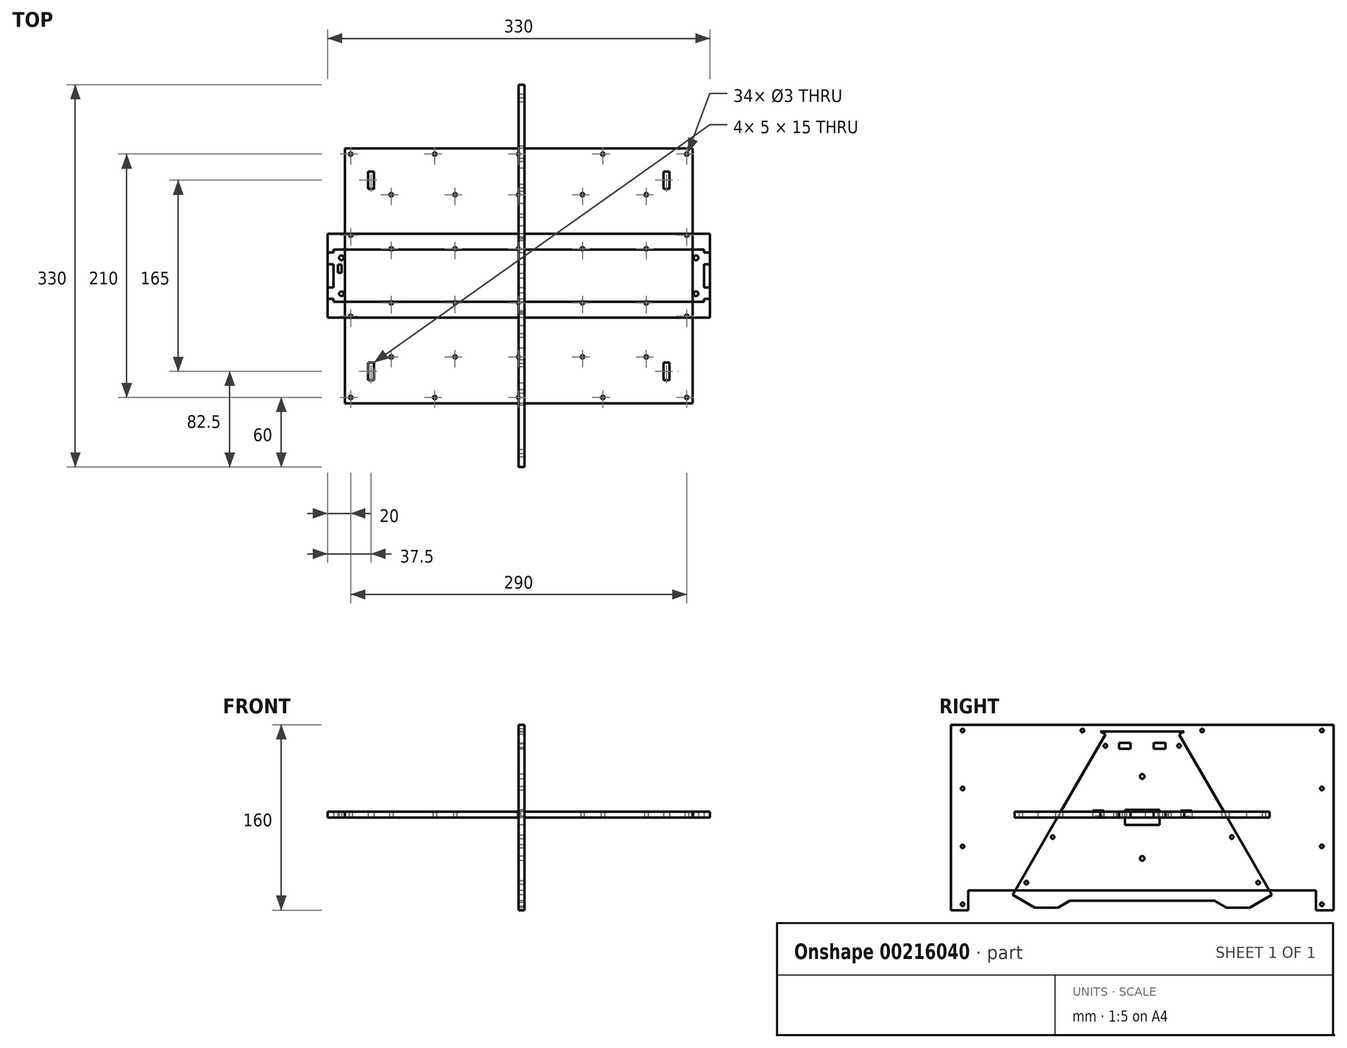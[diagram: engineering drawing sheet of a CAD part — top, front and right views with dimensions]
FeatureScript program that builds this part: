
annotation { "Feature Type Name" : "Feature", "Feature Type Description" : "" }
export const myFeature = defineFeature(function(context is Context, id is Id, definition is map)
    precondition{}
    {
        {
            var Q0;
            Q0=qCreatedBy(makeId("Top.planeOp"),FACE);
            var sketch = newSketch(context, id + "F0", { "sketchPlane" : qUnion([Q0])});
            skLineSegment(sketch, "E0.bottom", {"start": v(150, -110) * mm, "end": v(-150, -110) * mm});
            skLineSegment(sketch, "E0.top", {"start": v(150, 110) * mm, "end": v(-150, 110) * mm});
            skLineSegment(sketch, "E0.left", {"start": v(150, -110) * mm, "end": v(150, 110) * mm});
            skLineSegment(sketch, "E0.right", {"start": v(-150, -110) * mm, "end": v(-150, 110) * mm});
            skPoint(sketch, "E0.middle", {"position": v(0, 0) * mm});
            skCircle(sketch, "E1", {"center": v(-145, 105) * mm, "radius": 1.5 * mm});
            skCircle(sketch, "E2.0.1.0", {"center": v(-145, -105) * mm, "radius": 1.5 * mm});
            skCircle(sketch, "E2.1.0.0", {"center": v(-72.5, 105) * mm, "radius": 1.5 * mm});
            skCircle(sketch, "E2.1.1.0", {"center": v(-72.5, -105) * mm, "radius": 1.5 * mm});
            skCircle(sketch, "E2.2.0.0", {"center": v(0, 105) * mm, "radius": 1.5 * mm});
            skCircle(sketch, "E2.2.1.0", {"center": v(0, -105) * mm, "radius": 1.5 * mm});
            skCircle(sketch, "E2.3.0.0", {"center": v(72.5, 105) * mm, "radius": 1.5 * mm});
            skCircle(sketch, "E2.3.1.0", {"center": v(72.5, -105) * mm, "radius": 1.5 * mm});
            skCircle(sketch, "E2.4.0.0", {"center": v(145, 105) * mm, "radius": 1.5 * mm});
            skCircle(sketch, "E2.4.1.0", {"center": v(145, -105) * mm, "radius": 1.5 * mm});
            skLineSegment(sketch, "E2.direction1", {"start": v(-145, 105) * mm, "end": v(-72.5, 105) * mm, "construction": true});
            skLineSegment(sketch, "E2.direction2", {"start": v(-145, 105) * mm, "end": v(-145, -105) * mm, "construction": true});
            skCircle(sketch, "E3", {"center": v(-145, -35) * mm, "radius": 1.5 * mm});
            skCircle(sketch, "E4.0.1.0", {"center": v(-145, 35) * mm, "radius": 1.5 * mm});
            skCircle(sketch, "E4.1.0.0", {"center": v(145, -35) * mm, "radius": 1.5 * mm});
            skCircle(sketch, "E4.1.1.0", {"center": v(145, 35) * mm, "radius": 1.5 * mm});
            skLineSegment(sketch, "E4.direction1", {"start": v(-145, -35) * mm, "end": v(145, -35) * mm, "construction": true});
            skLineSegment(sketch, "E4.direction2", {"start": v(-145, -35) * mm, "end": v(-145, 35) * mm, "construction": true});
            skLineSegment(sketch, "E5", {"start": v(-87.87, 0) * mm, "end": v(86.7, 0) * mm, "construction": true});
            skLineSegment(sketch, "E6", {"start": v(0, -57.45) * mm, "end": v(0, 56.94) * mm, "construction": true});
            skLineSegment(sketch, "E7", {"start": v(145, 35) * mm, "end": v(145, 105) * mm, "construction": true});
            skLineSegment(sketch, "E8.bottom", {"start": v(-130, -75) * mm, "end": v(-125, -75) * mm});
            skLineSegment(sketch, "E8.top", {"start": v(-130, -90) * mm, "end": v(-125, -90) * mm});
            skLineSegment(sketch, "E8.left", {"start": v(-130, -75) * mm, "end": v(-130, -90) * mm});
            skLineSegment(sketch, "E8.right", {"start": v(-125, -75) * mm, "end": v(-125, -90) * mm});
            skLineSegment(sketch, "E9.0.1.0", {"start": v(-130, 90) * mm, "end": v(-130, 75) * mm});
            skLineSegment(sketch, "E9.0.1.1", {"start": v(-130, 75) * mm, "end": v(-125, 75) * mm});
            skLineSegment(sketch, "E9.0.1.2", {"start": v(-125, 90) * mm, "end": v(-125, 75) * mm});
            skLineSegment(sketch, "E9.0.1.3", {"start": v(-130, 90) * mm, "end": v(-125, 90) * mm});
            skLineSegment(sketch, "E9.1.0.0", {"start": v(125, -75) * mm, "end": v(125, -90) * mm});
            skLineSegment(sketch, "E9.1.0.1", {"start": v(125, -90) * mm, "end": v(130, -90) * mm});
            skLineSegment(sketch, "E9.1.0.2", {"start": v(130, -75) * mm, "end": v(130, -90) * mm});
            skLineSegment(sketch, "E9.1.0.3", {"start": v(125, -75) * mm, "end": v(130, -75) * mm});
            skLineSegment(sketch, "E9.1.1.0", {"start": v(125, 90) * mm, "end": v(125, 75) * mm});
            skLineSegment(sketch, "E9.1.1.1", {"start": v(125, 75) * mm, "end": v(130, 75) * mm});
            skLineSegment(sketch, "E9.1.1.2", {"start": v(130, 90) * mm, "end": v(130, 75) * mm});
            skLineSegment(sketch, "E9.1.1.3", {"start": v(125, 90) * mm, "end": v(130, 90) * mm});
            skLineSegment(sketch, "E9.direction1", {"start": v(-130, -90) * mm, "end": v(125, -90) * mm, "construction": true});
            skLineSegment(sketch, "E9.direction2", {"start": v(-130, -90) * mm, "end": v(-130, 75) * mm, "construction": true});
            skCircle(sketch, "E10", {"center": v(-110, 70) * mm, "radius": 1.5 * mm});
            skCircle(sketch, "E11.0.1.0", {"center": v(-110, 23.33) * mm, "radius": 1.5 * mm});
            skCircle(sketch, "E11.0.2.0", {"center": v(-110, -23.33) * mm, "radius": 1.5 * mm});
            skCircle(sketch, "E11.0.3.0", {"center": v(-110, -70) * mm, "radius": 1.5 * mm});
            skCircle(sketch, "E11.1.0.0", {"center": v(-55, 70) * mm, "radius": 1.5 * mm});
            skCircle(sketch, "E11.1.1.0", {"center": v(-55, 23.33) * mm, "radius": 1.5 * mm});
            skCircle(sketch, "E11.1.2.0", {"center": v(-55, -23.33) * mm, "radius": 1.5 * mm});
            skCircle(sketch, "E11.1.3.0", {"center": v(-55, -70) * mm, "radius": 1.5 * mm});
            skCircle(sketch, "E11.2.0.0", {"center": v(0, 70) * mm, "radius": 1.5 * mm});
            skCircle(sketch, "E11.2.1.0", {"center": v(0, 23.33) * mm, "radius": 1.5 * mm});
            skCircle(sketch, "E11.2.2.0", {"center": v(0, -23.33) * mm, "radius": 1.5 * mm});
            skCircle(sketch, "E11.2.3.0", {"center": v(0, -70) * mm, "radius": 1.5 * mm});
            skCircle(sketch, "E11.3.0.0", {"center": v(55, 70) * mm, "radius": 1.5 * mm});
            skCircle(sketch, "E11.3.1.0", {"center": v(55, 23.33) * mm, "radius": 1.5 * mm});
            skCircle(sketch, "E11.3.2.0", {"center": v(55, -23.33) * mm, "radius": 1.5 * mm});
            skCircle(sketch, "E11.3.3.0", {"center": v(55, -70) * mm, "radius": 1.5 * mm});
            skCircle(sketch, "E11.4.0.0", {"center": v(110, 70) * mm, "radius": 1.5 * mm});
            skCircle(sketch, "E11.4.1.0", {"center": v(110, 23.33) * mm, "radius": 1.5 * mm});
            skCircle(sketch, "E11.4.2.0", {"center": v(110, -23.33) * mm, "radius": 1.5 * mm});
            skCircle(sketch, "E11.4.3.0", {"center": v(110, -70) * mm, "radius": 1.5 * mm});
            skLineSegment(sketch, "E11.direction1", {"start": v(-110, 70) * mm, "end": v(-55, 70) * mm, "construction": true});
            skLineSegment(sketch, "E11.direction2", {"start": v(-110, 70) * mm, "end": v(-110, 23.33) * mm, "construction": true});
            skSolve(sketch);
        }
        {
            var Q0;
            Q0=makeQuery(id+"F0.imprint","IMPRINT",FACE,{"disambiguationData":[TD([[makeQuery(id+"F0.imprint","IMPRINT",EDGE,{"derivedFrom":sQuery(id+"F0.wireOp",EDGE,"E0.bottom")}),-1.0]])]});
            extrude(context, id + "F1", {"entities" : qUnion([Q0]), "depth" : 5 * mm});
        }
        {
            var Q0;
            Q0=qCreatedBy(makeId("Right.planeOp"),FACE);
            var sketch = newSketch(context, id + "F2", { "sketchPlane" : qUnion([Q0])});
            skLineSegment(sketch, "E12", {"start": v(-31.8, 71.78) * mm, "end": v(31.8, 71.78) * mm});
            skLineSegment(sketch, "E13", {"start": v(31.8, 71.78) * mm, "end": v(111.83, -66.78) * mm});
            skLineSegment(sketch, "E14", {"start": v(111.83, -66.78) * mm, "end": v(103.17, -71.78) * mm});
            skLineSegment(sketch, "E15", {"start": v(103.17, -71.78) * mm, "end": v(-103.17, -71.78) * mm});
            skLineSegment(sketch, "E16", {"start": v(-103.17, -71.78) * mm, "end": v(-111.83, -66.78) * mm});
            skLineSegment(sketch, "E17", {"start": v(-111.83, -66.78) * mm, "end": v(-31.8, 71.78) * mm});
            skLineSegment(sketch, "E18", {"start": v(0, -71.78) * mm, "end": v(0, 71.78) * mm, "construction": true});
            skCircle(sketch, "E19", {"center": v(31.8, 61.78) * mm, "radius": 1.5 * mm});
            skLineSegment(sketch, "E20", {"start": v(31.8, 61.78) * mm, "end": v(36.13, 64.28) * mm, "construction": true});
            skCircle(sketch, "E21.1.0.0", {"center": v(54.54, 22.43) * mm, "radius": 1.5 * mm, "construction": true});
            skCircle(sketch, "E21.2.0.0", {"center": v(77.27, -16.93) * mm, "radius": 1.5 * mm});
            skCircle(sketch, "E21.3.0.0", {"center": v(100, -56.3) * mm, "radius": 1.5 * mm});
            skLineSegment(sketch, "E21.direction1", {"start": v(31.8, 61.78) * mm, "end": v(54.54, 22.43) * mm, "construction": true});
            skLineSegment(sketch, "E22", {"start": v(100, -56.3) * mm, "end": v(107.5, -69.28) * mm, "construction": true});
            skCircle(sketch, "E23", {"center": v(-31.8, 61.78) * mm, "radius": 1.5 * mm});
            skCircle(sketch, "E24.1.0.0", {"center": v(-54.54, 22.43) * mm, "radius": 1.5 * mm, "construction": true});
            skCircle(sketch, "E24.2.0.0", {"center": v(-77.27, -16.93) * mm, "radius": 1.5 * mm});
            skCircle(sketch, "E24.3.0.0", {"center": v(-100, -56.3) * mm, "radius": 1.5 * mm});
            skLineSegment(sketch, "E24.direction1", {"start": v(-31.8, 61.78) * mm, "end": v(-54.54, 22.43) * mm, "construction": true});
            skLineSegment(sketch, "E25", {"start": v(-100, -56.3) * mm, "end": v(-107.5, -69.28) * mm, "construction": true});
            skCircle(sketch, "E26", {"center": v(0, 0) * mm, "radius": 35.35 * mm, "construction": true});
            skCircle(sketch, "E27", {"center": v(0, 35.35) * mm, "radius": 2 * mm});
            skCircle(sketch, "E28", {"center": v(0, -35.35) * mm, "radius": 2 * mm});
            skLineSegment(sketch, "E29", {"start": v(-103.17, -71.78) * mm, "end": v(-92.78, -77.78) * mm});
            skLineSegment(sketch, "E30", {"start": v(-92.78, -77.78) * mm, "end": v(-72.78, -77.78) * mm});
            skLineSegment(sketch, "E31", {"start": v(-72.78, -77.78) * mm, "end": v(-62.4, -71.78) * mm});
            skLineSegment(sketch, "E32", {"start": v(103.17, -71.78) * mm, "end": v(92.78, -77.78) * mm});
            skLineSegment(sketch, "E33", {"start": v(92.78, -77.78) * mm, "end": v(72.78, -77.78) * mm});
            skLineSegment(sketch, "E34", {"start": v(72.78, -77.78) * mm, "end": v(62.4, -71.78) * mm});
            skLineSegment(sketch, "E35", {"start": v(-31.8, 71.78) * mm, "end": v(-36.13, 74.28) * mm});
            skLineSegment(sketch, "E36", {"start": v(31.8, 71.78) * mm, "end": v(36.13, 74.28) * mm});
            skLineSegment(sketch, "E37", {"start": v(-36.13, 74.28) * mm, "end": v(36.13, 74.28) * mm});
            skLineSegment(sketch, "E38.bottom", {"start": v(33, 6) * mm, "end": v(43, 6) * mm});
            skLineSegment(sketch, "E38.top", {"start": v(33, 1) * mm, "end": v(43, 1) * mm});
            skLineSegment(sketch, "E38.left", {"start": v(33, 6) * mm, "end": v(33, 1) * mm});
            skLineSegment(sketch, "E38.right", {"start": v(43, 6) * mm, "end": v(43, 1) * mm});
            skLineSegment(sketch, "E39.bottom", {"start": v(-33, 6) * mm, "end": v(-43, 6) * mm});
            skLineSegment(sketch, "E39.top", {"start": v(-33, 1) * mm, "end": v(-43, 1) * mm});
            skLineSegment(sketch, "E39.left", {"start": v(-33, 6) * mm, "end": v(-33, 1) * mm});
            skLineSegment(sketch, "E39.right", {"start": v(-43, 6) * mm, "end": v(-43, 1) * mm});
            skLineSegment(sketch, "E40", {"start": v(-23.31, 0) * mm, "end": v(25.56, 0) * mm, "construction": true});
            skLineSegment(sketch, "E41.bottom", {"start": v(15, -6.5) * mm, "end": v(-15, -6.5) * mm});
            skLineSegment(sketch, "E41.top", {"start": v(15, 6.5) * mm, "end": v(-15, 6.5) * mm});
            skLineSegment(sketch, "E41.left", {"start": v(15, -6.5) * mm, "end": v(15, 6.5) * mm});
            skLineSegment(sketch, "E41.right", {"start": v(-15, -6.5) * mm, "end": v(-15, 6.5) * mm});
            skLineSegment(sketch, "E42.bottom", {"start": v(-15, -6.5) * mm, "end": v(-4, -6.5) * mm});
            skLineSegment(sketch, "E42.top", {"start": v(-15, 0) * mm, "end": v(-4, 0) * mm});
            skLineSegment(sketch, "E42.left", {"start": v(-15, -6.5) * mm, "end": v(-15, 0) * mm});
            skLineSegment(sketch, "E42.right", {"start": v(-4, -6.5) * mm, "end": v(-4, 0) * mm});
            skSolve(sketch);
        }
        {
            var Q0;
            Q0=makeQuery(id+"F2.imprint","IMPRINT",FACE,{"disambiguationData":[TD([[makeQuery(id+"F2.imprint","IMPRINT",EDGE,{"derivedFrom":sQuery(id+"F2.wireOp",EDGE,"E12")}),-1.0]])]});
            var Q1;
            {var subQ0=sQuery(id+"F2.wireOp",EDGE,"E29");Q1=makeQuery(id+"F2.imprint","IMPRINT",FACE,{"disambiguationData":[TD([[makeQuery(id+"F2.imprint","IMPRINT",EDGE,{"derivedFrom":subQ0}),1.0]])]});}
            var Q2;
            {var subQ0=sQuery(id+"F2.wireOp",EDGE,"E32");Q2=makeQuery(id+"F2.imprint","IMPRINT",FACE,{"disambiguationData":[TD([[makeQuery(id+"F2.imprint","IMPRINT",EDGE,{"derivedFrom":subQ0}),-1.0]])]});}
            var Q3;
            Q3=makeQuery(id+"F2.imprint","IMPRINT",FACE,{"disambiguationData":[TD([[makeQuery(id+"F2.imprint","IMPRINT",EDGE,{"derivedFrom":sQuery(id+"F2.wireOp",EDGE,"E12")}),1.0]])]});
            var Q4;
            Q4=makeQuery(id+"F2.imprint","IMPRINT",FACE,{"disambiguationData":[TD([[makeQuery(id+"F2.imprint","IMPRINT",EDGE,{"derivedFrom":sQuery(id+"F2.wireOp",EDGE,"1zBQG6Iy-hJ6P-1aGQ-Iii5-wYXhp56Ifulz.bottom")}),-1.0]])]});
            var Q5;
            Q5=makeQuery(id+"F2.imprint","IMPRINT",FACE,{"disambiguationData":[TD([[makeQuery(id+"F2.imprint","IMPRINT",EDGE,{"derivedFrom":sQuery(id+"F2.wireOp",EDGE,"E42.bottom")}),1.0]])]});
            extrude(context, id + "F3", {"entities" : qUnion([Q0, Q1, Q2, Q3, Q4, Q5]), "depth" : 5 * mm});
        }
        {
            var Q0;
            Q0=qCreatedBy(makeId("Right.planeOp"),FACE);
            var sketch = newSketch(context, id + "F4", { "sketchPlane" : qUnion([Q0])});
            skLineSegment(sketch, "E43", {"start": v(-165, 80) * mm, "end": v(165, 80) * mm});
            skLineSegment(sketch, "E44", {"start": v(165, 80) * mm, "end": v(165, -80) * mm});
            skLineSegment(sketch, "E45", {"start": v(165, -80) * mm, "end": v(150, -80) * mm});
            skLineSegment(sketch, "E46", {"start": v(150, -80) * mm, "end": v(150, -63) * mm});
            skLineSegment(sketch, "E47", {"start": v(150, -63) * mm, "end": v(-150, -63) * mm});
            skLineSegment(sketch, "E48", {"start": v(-150, -63) * mm, "end": v(-150, -80) * mm});
            skLineSegment(sketch, "E49", {"start": v(-150, -80) * mm, "end": v(-165, -80) * mm});
            skLineSegment(sketch, "E50", {"start": v(-165, -80) * mm, "end": v(-165, 80) * mm});
            skLineSegment(sketch, "E51", {"start": v(0, 153.24) * mm, "end": v(0, -118.2) * mm, "construction": true});
            skLineSegment(sketch, "E52", {"start": v(-243.49, 0) * mm, "end": v(242.88, 0) * mm, "construction": true});
            skCircle(sketch, "E53", {"center": v(155, -75) * mm, "radius": 1.5 * mm});
            skCircle(sketch, "E54", {"center": v(-155, -75) * mm, "radius": 1.5 * mm});
            skCircle(sketch, "E55.1.0.0", {"center": v(155, -25) * mm, "radius": 1.5 * mm});
            skCircle(sketch, "E55.2.0.0", {"center": v(155, 25) * mm, "radius": 1.5 * mm});
            skCircle(sketch, "E55.3.0.0", {"center": v(155, 75) * mm, "radius": 1.5 * mm});
            skLineSegment(sketch, "E55.direction1", {"start": v(155, -75) * mm, "end": v(155, -25) * mm, "construction": true});
            skCircle(sketch, "E56.1.0.0", {"center": v(-155, -25) * mm, "radius": 1.5 * mm});
            skCircle(sketch, "E56.2.0.0", {"center": v(-155, 25) * mm, "radius": 1.5 * mm});
            skCircle(sketch, "E56.3.0.0", {"center": v(-155, 75) * mm, "radius": 1.5 * mm});
            skLineSegment(sketch, "E56.direction1", {"start": v(-155, -75) * mm, "end": v(-155, -25) * mm, "construction": true});
            skCircle(sketch, "E57.1.0.0", {"center": v(-51.67, 75) * mm, "radius": 1.5 * mm});
            skCircle(sketch, "E57.2.0.0", {"center": v(51.67, 75) * mm, "radius": 1.5 * mm});
            skLineSegment(sketch, "E57.direction1", {"start": v(-155, 75) * mm, "end": v(-51.67, 75) * mm, "construction": true});
            skLineSegment(sketch, "E58", {"start": v(51.67, 75) * mm, "end": v(155, 75) * mm, "construction": true});
            skSolve(sketch);
        }
        {
            var Q0;
            Q0=makeQuery(id+"F4.imprint","IMPRINT",FACE,{"disambiguationData":[TD([[makeQuery(id+"F4.imprint","IMPRINT",EDGE,{"derivedFrom":sQuery(id+"F4.wireOp",EDGE,"E43")}),-1.0]])]});
            extrude(context, id + "F5", {"entities" : qUnion([Q0]), "depth" : 5 * mm});
        }
        {
            var Q0;
            Q0=makeQuery(id+"F3.opExtrude","CAP_FACE",FACE,{"disambiguationData":[OSD([sQuery(id+"F2.wireOp",EDGE,"E13"),sQuery(id+"F2.wireOp",EDGE,"E14"),sQuery(id+"F2.wireOp",EDGE,"E15"),sQuery(id+"F2.wireOp",EDGE,"E16"),sQuery(id+"F2.wireOp",EDGE,"E17"),sQuery(id+"F2.wireOp",EDGE,"E19"),sQuery(id+"F2.wireOp",EDGE,"E21.2.0.0"),sQuery(id+"F2.wireOp",EDGE,"E21.3.0.0"),sQuery(id+"F2.wireOp",EDGE,"E23"),sQuery(id+"F2.wireOp",EDGE,"E24.2.0.0"),sQuery(id+"F2.wireOp",EDGE,"E24.3.0.0"),sQuery(id+"F2.wireOp",EDGE,"O3QZEwBj-KtqO-yXGe-cdQq-akg9gxT5v1oA"),sQuery(id+"F2.wireOp",EDGE,"E27"),sQuery(id+"F2.wireOp",EDGE,"E28"),sQuery(id+"F2.wireOp",EDGE,"E29"),sQuery(id+"F2.wireOp",EDGE,"E30"),sQuery(id+"F2.wireOp",EDGE,"E31"),sQuery(id+"F2.wireOp",EDGE,"E32"),sQuery(id+"F2.wireOp",EDGE,"E33"),sQuery(id+"F2.wireOp",EDGE,"E34"),sQuery(id+"F2.wireOp",EDGE,"E35"),sQuery(id+"F2.wireOp",EDGE,"E36"),sQuery(id+"F2.wireOp",EDGE,"E37")])],"isStart":false});
            var sketch = newSketch(context, id + "F6", { "sketchPlane" : qUnion([Q0])});
            skLineSegment(sketch, "E59.bottom", {"start": v(10, 64.28) * mm, "end": v(20, 64.28) * mm});
            skLineSegment(sketch, "E59.top", {"start": v(10, 59.28) * mm, "end": v(20, 59.28) * mm});
            skLineSegment(sketch, "E59.left", {"start": v(10, 64.28) * mm, "end": v(10, 59.28) * mm});
            skLineSegment(sketch, "E59.right", {"start": v(20, 64.28) * mm, "end": v(20, 59.28) * mm});
            skLineSegment(sketch, "E60.bottom", {"start": v(-20, 64.28) * mm, "end": v(-10, 64.28) * mm});
            skLineSegment(sketch, "E60.top", {"start": v(-20, 59.28) * mm, "end": v(-10, 59.28) * mm});
            skLineSegment(sketch, "E60.left", {"start": v(-20, 64.28) * mm, "end": v(-20, 59.28) * mm});
            skLineSegment(sketch, "E60.right", {"start": v(-10, 64.28) * mm, "end": v(-10, 59.28) * mm});
            skLineSegment(sketch, "E61", {"start": v(0, 106.18) * mm, "end": v(0, 6.84) * mm, "construction": true});
            skSolve(sketch);
        }
        {
            var Q0;
            Q0=makeQuery(id+"F6.imprint","IMPRINT",FACE,{"disambiguationData":[TD([[makeQuery(id+"F6.imprint","IMPRINT",EDGE,{"derivedFrom":sQuery(id+"F6.wireOp",EDGE,"E59.bottom")}),-1.0]])]});
            var Q1;
            Q1=makeQuery(id+"F6.imprint","IMPRINT",FACE,{"disambiguationData":[TD([[makeQuery(id+"F6.imprint","IMPRINT",EDGE,{"derivedFrom":sQuery(id+"F6.wireOp",EDGE,"E60.bottom")}),-1.0]])]});
            extrude(context, id + "F7", {"entities" : qUnion([Q0, Q1]), "operationType" : NewBodyOperationType.REMOVE, "endBound" : BoundingType.THROUGH_ALL, "oppositeDirection" : true, "depth" : 25 * mm});
        }
        {
            var Q0;
            Q0=qCreatedBy(makeId("Top.planeOp"),FACE);
            var sketch = newSketch(context, id + "F10", { "sketchPlane" : qUnion([Q0])});
            skLineSegment(sketch, "E62.bottom", {"start": v(160, -22.5) * mm, "end": v(-160, -22.5) * mm});
            skLineSegment(sketch, "E62.top", {"start": v(160, 22.5) * mm, "end": v(-160, 22.5) * mm});
            skLineSegment(sketch, "E62.left", {"start": v(160, -22.5) * mm, "end": v(160, 22.5) * mm});
            skLineSegment(sketch, "E62.right", {"start": v(-160, -22.5) * mm, "end": v(-160, 22.5) * mm});
            skPoint(sketch, "E62.middle", {"position": v(0, 0) * mm});
            skLineSegment(sketch, "E63", {"start": v(160, 20) * mm, "end": v(165, 20) * mm});
            skLineSegment(sketch, "E64", {"start": v(165, 20) * mm, "end": v(165, 10) * mm});
            skLineSegment(sketch, "E65", {"start": v(165, 10) * mm, "end": v(160, 10) * mm});
            skLineSegment(sketch, "E66", {"start": v(160, -10) * mm, "end": v(165, -10) * mm});
            skLineSegment(sketch, "E67", {"start": v(165, -10) * mm, "end": v(165, -20) * mm});
            skLineSegment(sketch, "E68", {"start": v(165, -20) * mm, "end": v(160, -20) * mm});
            skLineSegment(sketch, "E69", {"start": v(-160, 20) * mm, "end": v(-165, 20) * mm});
            skLineSegment(sketch, "E70", {"start": v(-165, 20) * mm, "end": v(-165, 10) * mm});
            skLineSegment(sketch, "E71", {"start": v(-165, 10) * mm, "end": v(-160, 10) * mm});
            skLineSegment(sketch, "E72", {"start": v(-160, -10) * mm, "end": v(-165, -10) * mm});
            skLineSegment(sketch, "E73", {"start": v(-165, -10) * mm, "end": v(-165, -20) * mm});
            skLineSegment(sketch, "E74", {"start": v(-165, -20) * mm, "end": v(-160, -20) * mm});
            skLineSegment(sketch, "E75", {"start": v(-87.24, 0) * mm, "end": v(82.04, 0) * mm, "construction": true});
            skCircle(sketch, "E76", {"center": v(-153, 15.5) * mm, "radius": 2 * mm});
            skCircle(sketch, "E77", {"center": v(-153, -15.5) * mm, "radius": 2 * mm});
            skCircle(sketch, "E78", {"center": v(153, 15.5) * mm, "radius": 2 * mm});
            skCircle(sketch, "E79", {"center": v(153, -15.5) * mm, "radius": 2 * mm});
            skLineSegment(sketch, "E80.bottom", {"start": v(-156, 9.5) * mm, "end": v(-153, 9.5) * mm});
            skLineSegment(sketch, "E80.top", {"start": v(-156, 2.5) * mm, "end": v(-153, 2.5) * mm});
            skLineSegment(sketch, "E80.left", {"start": v(-156, 9.5) * mm, "end": v(-156, 2.5) * mm});
            skLineSegment(sketch, "E80.right", {"start": v(-153, 9.5) * mm, "end": v(-153, 2.5) * mm});
            skSolve(sketch);
        }
        {
            var Q0;
            Q0 = qSketchRegion(id + "F10", true);
            extrude(context, id + "F8", {"entities" : qUnion([Q0]), "depth" : 5 * mm});
        }
        {
            var Q0;
            Q0=qCreatedBy(makeId("Top.planeOp"),FACE);
            var sketch = newSketch(context, id + "F11", { "sketchPlane" : qUnion([Q0])});
            skLineSegment(sketch, "E81.bottom", {"start": v(165, 36.13) * mm, "end": v(-165, 36.13) * mm});
            skLineSegment(sketch, "E81.top", {"start": v(165, -36.13) * mm, "end": v(-165, -36.13) * mm});
            skLineSegment(sketch, "E81.left", {"start": v(165, 36.13) * mm, "end": v(165, -36.13) * mm});
            skLineSegment(sketch, "E81.right", {"start": v(-165, 36.13) * mm, "end": v(-165, -36.13) * mm});
            skPoint(sketch, "E81.middle", {"position": v(0, 0) * mm});
            skCircle(sketch, "E82", {"center": v(-153, 15.5) * mm, "radius": 2 * mm});
            skCircle(sketch, "E83", {"center": v(-153, -15.5) * mm, "radius": 2 * mm});
            skCircle(sketch, "E84", {"center": v(153, 15.5) * mm, "radius": 2 * mm});
            skCircle(sketch, "E85", {"center": v(153, -15.5) * mm, "radius": 2 * mm});
            skLineSegment(sketch, "E86", {"start": v(-124.87, 0) * mm, "end": v(137.78, 0) * mm, "construction": true});
            skSolve(sketch);
        }
        {
            var Q0;
            Q0 = qSketchRegion(id + "F11", true);
            extrude(context, id + "F9", {"entities" : qUnion([Q0]), "depth" : 5 * mm});
        }
    });
